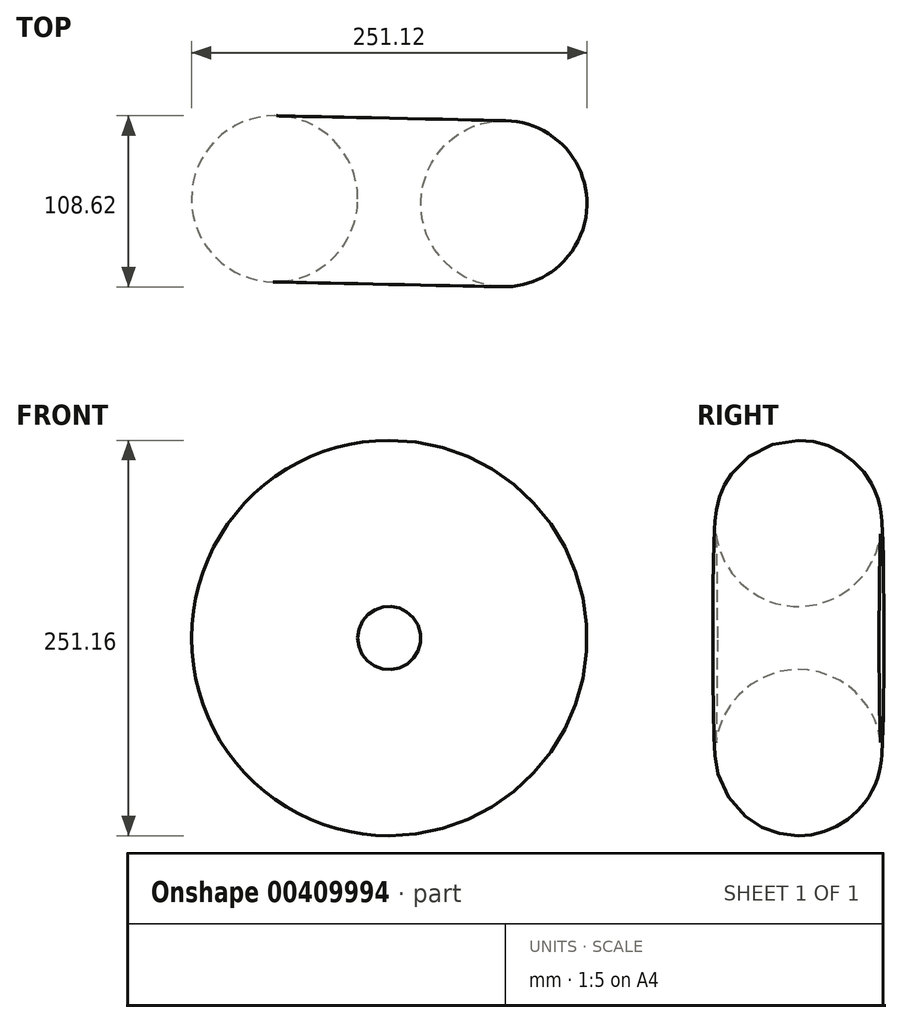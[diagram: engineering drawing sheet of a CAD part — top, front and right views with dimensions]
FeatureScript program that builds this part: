
annotation { "Feature Type Name" : "Feature", "Feature Type Description" : "" }
export const myFeature = defineFeature(function(context is Context, id is Id, definition is map)
    precondition{}
    {
        {
            var Q0;
            Q0=qCreatedBy(makeId("Top.planeOp"),FACE);
            var sketch = newSketch(context, id + "F0", { "sketchPlane" : qUnion([Q0])});
            skCircle(sketch, "E0", {"center": v(0, -10.02) * mm, "radius": 52.77 * mm});
            skCircle(sketch, "E1.cCircle", {"center": v(-20.6, 13.6) * mm, "radius": 6.7 * mm, "construction": true});
            skLineSegment(sketch, "E1.0", {"start": v(-15.87, 18.33) * mm, "end": v(-18.86, 7.13) * mm});
            skLineSegment(sketch, "E1.1", {"start": v(-18.86, 7.13) * mm, "end": v(-27.07, 15.33) * mm});
            skLineSegment(sketch, "E1.2", {"start": v(-27.07, 15.33) * mm, "end": v(-15.87, 18.33) * mm});
            skCircle(sketch, "E2.cCircle", {"center": v(-4.45, 30.32) * mm, "radius": 6.96 * mm, "construction": true});
            skLineSegment(sketch, "E2.0", {"start": v(-2.5, 37) * mm, "end": v(0.36, 25.29) * mm});
            skLineSegment(sketch, "E2.1", {"start": v(0.36, 25.29) * mm, "end": v(-11.21, 28.66) * mm});
            skLineSegment(sketch, "E2.2", {"start": v(-11.21, 28.66) * mm, "end": v(-2.5, 37) * mm});
            skCircle(sketch, "E3.cCircle", {"center": v(3.9, 10.85) * mm, "radius": 7.52 * mm, "construction": true});
            skLineSegment(sketch, "E3.0", {"start": v(3.62, 18.37) * mm, "end": v(10.54, 7.34) * mm});
            skLineSegment(sketch, "E3.1", {"start": v(10.54, 7.34) * mm, "end": v(-2.47, 6.86) * mm});
            skLineSegment(sketch, "E3.2", {"start": v(-2.47, 6.86) * mm, "end": v(3.62, 18.37) * mm});
            skCircle(sketch, "E4.cCircle", {"center": v(25.6, 24.24) * mm, "radius": 6.3 * mm, "construction": true});
            skLineSegment(sketch, "E4.0", {"start": v(23.94, 30.32) * mm, "end": v(31.7, 22.65) * mm});
            skLineSegment(sketch, "E4.1", {"start": v(31.7, 22.65) * mm, "end": v(21.18, 19.76) * mm});
            skLineSegment(sketch, "E4.2", {"start": v(21.18, 19.76) * mm, "end": v(23.94, 30.32) * mm});
            skCircle(sketch, "E5.cCircle", {"center": v(26.44, 3.1) * mm, "radius": 7.15 * mm, "construction": true});
            skLineSegment(sketch, "E5.0", {"start": v(24.77, 10.05) * mm, "end": v(33.3, 1.07) * mm});
            skLineSegment(sketch, "E5.1", {"start": v(33.3, 1.07) * mm, "end": v(21.26, -1.82) * mm});
            skLineSegment(sketch, "E5.2", {"start": v(21.26, -1.82) * mm, "end": v(24.77, 10.05) * mm});
            skCircle(sketch, "E6.cCircle", {"center": v(-38.7, 0) * mm, "radius": 7.06 * mm, "construction": true});
            skLineSegment(sketch, "E6.0", {"start": v(-35.07, 6.06) * mm, "end": v(-35.25, -6.16) * mm});
            skLineSegment(sketch, "E6.1", {"start": v(-35.25, -6.16) * mm, "end": v(-45.75, 0.1) * mm});
            skLineSegment(sketch, "E6.2", {"start": v(-45.75, 0.1) * mm, "end": v(-35.07, 6.06) * mm});
            skCircle(sketch, "E7.cCircle", {"center": v(-13.08, -6.7) * mm, "radius": 6.9 * mm, "construction": true});
            skLineSegment(sketch, "E7.0", {"start": v(-11.41, 0) * mm, "end": v(-8.11, -11.5) * mm});
            skLineSegment(sketch, "E7.1", {"start": v(-8.11, -11.5) * mm, "end": v(-19.72, -8.6) * mm});
            skLineSegment(sketch, "E7.2", {"start": v(-19.72, -8.6) * mm, "end": v(-11.41, 0) * mm});
            skCircle(sketch, "E8.cCircle", {"center": v(-29.5, -21.47) * mm, "radius": 7.05 * mm, "construction": true});
            skLineSegment(sketch, "E8.0", {"start": v(-28.4, -14.52) * mm, "end": v(-24.04, -25.92) * mm});
            skLineSegment(sketch, "E8.1", {"start": v(-24.04, -25.92) * mm, "end": v(-36.09, -23.99) * mm});
            skLineSegment(sketch, "E8.2", {"start": v(-36.09, -23.99) * mm, "end": v(-28.4, -14.52) * mm});
            skCircle(sketch, "E9.cCircle", {"center": v(14.2, -16.67) * mm, "radius": 8.28 * mm, "construction": true});
            skLineSegment(sketch, "E9.0", {"start": v(16.98, -8.88) * mm, "end": v(19.55, -22.98) * mm});
            skLineSegment(sketch, "E9.1", {"start": v(19.55, -22.98) * mm, "end": v(6.05, -18.16) * mm});
            skLineSegment(sketch, "E9.2", {"start": v(6.05, -18.16) * mm, "end": v(16.98, -8.88) * mm});
            skCircle(sketch, "E10.cCircle", {"center": v(-6.68, -28.4) * mm, "radius": 7.28 * mm, "construction": true});
            skLineSegment(sketch, "E10.0", {"start": v(-7.52, -21.16) * mm, "end": v(0, -31.29) * mm});
            skLineSegment(sketch, "E10.1", {"start": v(0, -31.29) * mm, "end": v(-12.53, -32.73) * mm});
            skLineSegment(sketch, "E10.2", {"start": v(-12.53, -32.73) * mm, "end": v(-7.52, -21.16) * mm});
            skCircle(sketch, "E11.cCircle", {"center": v(38.13, -14.69) * mm, "radius": 7.37 * mm, "construction": true});
            skLineSegment(sketch, "E11.0", {"start": v(39.53, -7.45) * mm, "end": v(43.7, -19.51) * mm});
            skLineSegment(sketch, "E11.1", {"start": v(43.7, -19.51) * mm, "end": v(31.17, -17.1) * mm});
            skLineSegment(sketch, "E11.2", {"start": v(31.17, -17.1) * mm, "end": v(39.53, -7.45) * mm});
            skCircle(sketch, "E12.cCircle", {"center": v(33.3, -36.4) * mm, "radius": 7.52 * mm, "construction": true});
            skLineSegment(sketch, "E12.0", {"start": v(33.3, -28.88) * mm, "end": v(39.8, -40.16) * mm});
            skLineSegment(sketch, "E12.1", {"start": v(39.8, -40.16) * mm, "end": v(26.8, -40.16) * mm});
            skLineSegment(sketch, "E12.2", {"start": v(26.8, -40.16) * mm, "end": v(33.3, -28.88) * mm});
            skCircle(sketch, "E13.cCircle", {"center": v(11.97, -37.82) * mm, "radius": 7.61 * mm, "construction": true});
            skLineSegment(sketch, "E13.0", {"start": v(15.87, -31.29) * mm, "end": v(15.68, -44.47) * mm});
            skLineSegment(sketch, "E13.1", {"start": v(15.68, -44.47) * mm, "end": v(4.36, -37.72) * mm});
            skLineSegment(sketch, "E13.2", {"start": v(4.36, -37.72) * mm, "end": v(15.87, -31.29) * mm});
            skCircle(sketch, "E14.cCircle", {"center": v(2.23, -54.8) * mm, "radius": 8.07 * mm, "construction": true});
            skLineSegment(sketch, "E14.0", {"start": v(2.23, -46.74) * mm, "end": v(9.21, -58.84) * mm});
            skLineSegment(sketch, "E14.1", {"start": v(9.21, -58.84) * mm, "end": v(-4.76, -58.84) * mm});
            skLineSegment(sketch, "E14.2", {"start": v(-4.76, -58.84) * mm, "end": v(2.23, -46.74) * mm});
            skCircle(sketch, "E15.cCircle", {"center": v(-14.47, -41.48) * mm, "radius": 6.13 * mm, "construction": true});
            skLineSegment(sketch, "E15.0", {"start": v(-14.2, -35.36) * mm, "end": v(-9.31, -44.78) * mm});
            skLineSegment(sketch, "E15.1", {"start": v(-9.31, -44.78) * mm, "end": v(-19.91, -44.3) * mm});
            skLineSegment(sketch, "E15.2", {"start": v(-19.91, -44.3) * mm, "end": v(-14.2, -35.36) * mm});
            skCircle(sketch, "E16.cCircle", {"center": v(-32.01, -37.06) * mm, "radius": 6 * mm, "construction": true});
            skLineSegment(sketch, "E16.0", {"start": v(-30.34, -31.29) * mm, "end": v(-27.85, -41.4) * mm});
            skLineSegment(sketch, "E16.1", {"start": v(-27.85, -41.4) * mm, "end": v(-37.84, -38.5) * mm});
            skLineSegment(sketch, "E16.2", {"start": v(-37.84, -38.5) * mm, "end": v(-30.34, -31.29) * mm});
            skCircle(sketch, "E17.cCircle", {"center": v(-35.07, 19.76) * mm, "radius": 4.62 * mm, "construction": true});
            skLineSegment(sketch, "E17.0", {"start": v(-33.96, 24.24) * mm, "end": v(-31.75, 16.56) * mm});
            skLineSegment(sketch, "E17.1", {"start": v(-31.75, 16.56) * mm, "end": v(-39.51, 18.48) * mm});
            skLineSegment(sketch, "E17.2", {"start": v(-39.51, 18.48) * mm, "end": v(-33.96, 24.24) * mm});
            skCircle(sketch, "E18.cCircle", {"center": v(-18.93, 30.85) * mm, "radius": 4.8 * mm, "construction": true});
            skLineSegment(sketch, "E18.0", {"start": v(-18.1, 35.58) * mm, "end": v(-15.25, 27.76) * mm});
            skLineSegment(sketch, "E18.1", {"start": v(-15.25, 27.76) * mm, "end": v(-23.44, 29.2) * mm});
            skLineSegment(sketch, "E18.2", {"start": v(-23.44, 29.2) * mm, "end": v(-18.1, 35.58) * mm});
            skCircle(sketch, "E19.cCircle", {"center": v(10.58, 27.56) * mm, "radius": 5.02 * mm, "construction": true});
            skLineSegment(sketch, "E19.0", {"start": v(10.86, 32.57) * mm, "end": v(14.78, 24.81) * mm});
            skLineSegment(sketch, "E19.1", {"start": v(14.78, 24.81) * mm, "end": v(6.1, 25.3) * mm});
            skLineSegment(sketch, "E19.2", {"start": v(6.1, 25.3) * mm, "end": v(10.86, 32.57) * mm});
            skCircle(sketch, "E20.cCircle", {"center": v(40.92, 5.9) * mm, "radius": 4.37 * mm, "construction": true});
            skLineSegment(sketch, "E20.0", {"start": v(39.53, 10.05) * mm, "end": v(45.2, 5.04) * mm});
            skLineSegment(sketch, "E20.1", {"start": v(45.2, 5.04) * mm, "end": v(38.02, 2.63) * mm});
            skLineSegment(sketch, "E20.2", {"start": v(38.02, 2.63) * mm, "end": v(39.53, 10.05) * mm});
            skCircle(sketch, "E21.cCircle", {"center": v(4.45, -3.06) * mm, "radius": 6.6 * mm, "construction": true});
            skLineSegment(sketch, "E21.0", {"start": v(10.3, 0) * mm, "end": v(4.18, -9.65) * mm});
            skLineSegment(sketch, "E21.1", {"start": v(4.18, -9.65) * mm, "end": v(-1.12, 0.48) * mm});
            skLineSegment(sketch, "E21.2", {"start": v(-1.12, 0.48) * mm, "end": v(10.3, 0) * mm});
            skCircle(sketch, "E22.cCircle", {"center": v(-45.1, -13.99) * mm, "radius": 6.35 * mm, "construction": true});
            skLineSegment(sketch, "E22.0", {"start": v(-43.42, -7.86) * mm, "end": v(-40.63, -18.5) * mm});
            skLineSegment(sketch, "E22.1", {"start": v(-40.63, -18.5) * mm, "end": v(-51.23, -15.6) * mm});
            skLineSegment(sketch, "E22.2", {"start": v(-51.23, -15.6) * mm, "end": v(-43.42, -7.86) * mm});
            skCircle(sketch, "E23.cCircle", {"center": v(21.18, -50.6) * mm, "radius": 6.12 * mm, "construction": true});
            skLineSegment(sketch, "E23.0", {"start": v(21.18, -44.48) * mm, "end": v(26.49, -53.67) * mm});
            skLineSegment(sketch, "E23.1", {"start": v(26.49, -53.67) * mm, "end": v(15.88, -53.67) * mm});
            skLineSegment(sketch, "E23.2", {"start": v(15.88, -53.67) * mm, "end": v(21.18, -44.48) * mm});
            skCircle(sketch, "E24.cCircle", {"center": v(-16.14, -53.17) * mm, "radius": 3.71 * mm, "construction": true});
            skLineSegment(sketch, "E24.0", {"start": v(-16.98, -49.55) * mm, "end": v(-12.6, -54.25) * mm});
            skLineSegment(sketch, "E24.1", {"start": v(-12.6, -54.25) * mm, "end": v(-18.86, -55.7) * mm});
            skLineSegment(sketch, "E24.2", {"start": v(-18.86, -55.7) * mm, "end": v(-16.98, -49.55) * mm});
            skLineSegment(sketch, "E25", {"start": v(-71.54, 50.8) * mm, "end": v(-73.76, -54.65) * mm});
            skSolve(sketch);
        }
        {
            var Q0;
            Q0=makeQuery(id+"F0.imprint","IMPRINT",FACE,{"disambiguationData":[TD([[makeQuery(id+"F0.imprint","IMPRINT",EDGE,{"derivedFrom":sQuery(id+"F0.wireOp",EDGE,"E2.0")}),-1.0]])]});
            var Q1;
            Q1=makeQuery(id+"F0.imprint","IMPRINT",FACE,{"disambiguationData":[TD([[makeQuery(id+"F0.imprint","IMPRINT",EDGE,{"derivedFrom":sQuery(id+"F0.wireOp",EDGE,"E3.0")}),-1.0]])]});
            var Q2;
            Q2=makeQuery(id+"F0.imprint","IMPRINT",FACE,{"disambiguationData":[TD([[makeQuery(id+"F0.imprint","IMPRINT",EDGE,{"derivedFrom":sQuery(id+"F0.wireOp",EDGE,"E13.0")}),-1.0]])]});
            var Q3;
            Q3=makeQuery(id+"F0.imprint","IMPRINT",FACE,{"disambiguationData":[TD([[makeQuery(id+"F0.imprint","IMPRINT",EDGE,{"derivedFrom":sQuery(id+"F0.wireOp",EDGE,"E12.0")}),-1.0]])]});
            var Q4;
            Q4=makeQuery(id+"F0.imprint","IMPRINT",FACE,{"disambiguationData":[TD([[makeQuery(id+"F0.imprint","IMPRINT",EDGE,{"derivedFrom":sQuery(id+"F0.wireOp",EDGE,"E11.0")}),-1.0]])]});
            var Q5;
            Q5=makeQuery(id+"F0.imprint","IMPRINT",FACE,{"disambiguationData":[TD([[makeQuery(id+"F0.imprint","IMPRINT",EDGE,{"derivedFrom":sQuery(id+"F0.wireOp",EDGE,"E10.0")}),-1.0]])]});
            var Q6;
            Q6=makeQuery(id+"F0.imprint","IMPRINT",FACE,{"disambiguationData":[TD([[makeQuery(id+"F0.imprint","IMPRINT",EDGE,{"derivedFrom":sQuery(id+"F0.wireOp",EDGE,"E9.0")}),-1.0]])]});
            var Q7;
            Q7=makeQuery(id+"F0.imprint","IMPRINT",FACE,{"disambiguationData":[TD([[makeQuery(id+"F0.imprint","IMPRINT",EDGE,{"derivedFrom":sQuery(id+"F0.wireOp",EDGE,"E8.0")}),-1.0]])]});
            var Q8;
            Q8=makeQuery(id+"F0.imprint","IMPRINT",FACE,{"disambiguationData":[TD([[makeQuery(id+"F0.imprint","IMPRINT",EDGE,{"derivedFrom":sQuery(id+"F0.wireOp",EDGE,"E7.0")}),-1.0]])]});
            var Q9;
            Q9=makeQuery(id+"F0.imprint","IMPRINT",FACE,{"disambiguationData":[TD([[makeQuery(id+"F0.imprint","IMPRINT",EDGE,{"derivedFrom":sQuery(id+"F0.wireOp",EDGE,"E1.0")}),-1.0]])]});
            var Q10;
            Q10=makeQuery(id+"F0.imprint","IMPRINT",FACE,{"disambiguationData":[TD([[makeQuery(id+"F0.imprint","IMPRINT",EDGE,{"derivedFrom":sQuery(id+"F0.wireOp",EDGE,"E5.0")}),-1.0]])]});
            var Q11;
            Q11=makeQuery(id+"F0.imprint","IMPRINT",FACE,{"disambiguationData":[TD([[makeQuery(id+"F0.imprint","IMPRINT",EDGE,{"derivedFrom":sQuery(id+"F0.wireOp",EDGE,"E4.0")}),-1.0]])]});
            var Q12;
            Q12=makeQuery(id+"F0.imprint","IMPRINT",FACE,{"disambiguationData":[TD([[makeQuery(id+"F0.imprint","IMPRINT",EDGE,{"derivedFrom":sQuery(id+"F0.wireOp",EDGE,"E6.0")}),-1.0]])]});
            var Q13;
            Q13=makeQuery(id+"F0.imprint","IMPRINT",FACE,{"disambiguationData":[TD([[makeQuery(id+"F0.imprint","IMPRINT",EDGE,{"derivedFrom":sQuery(id+"F0.wireOp",EDGE,"E22.0")}),-1.0]])]});
            var Q14;
            Q14=makeQuery(id+"F0.imprint","IMPRINT",FACE,{"disambiguationData":[TD([[makeQuery(id+"F0.imprint","IMPRINT",EDGE,{"derivedFrom":sQuery(id+"F0.wireOp",EDGE,"E15.0")}),-1.0]])]});
            var Q15;
            Q15=makeQuery(id+"F0.imprint","IMPRINT",FACE,{"disambiguationData":[TD([[makeQuery(id+"F0.imprint","IMPRINT",EDGE,{"derivedFrom":sQuery(id+"F0.wireOp",EDGE,"E14.0")}),-1.0]])]});
            var Q16;
            Q16=makeQuery(id+"F0.imprint","IMPRINT",FACE,{"disambiguationData":[TD([[makeQuery(id+"F0.imprint","IMPRINT",EDGE,{"derivedFrom":sQuery(id+"F0.wireOp",EDGE,"E16.0")}),-1.0]])]});
            var Q17;
            Q17=makeQuery(id+"F0.imprint","IMPRINT",FACE,{"disambiguationData":[TD([[makeQuery(id+"F0.imprint","IMPRINT",EDGE,{"derivedFrom":sQuery(id+"F0.wireOp",EDGE,"E18.0")}),-1.0]])]});
            var Q18;
            Q18=makeQuery(id+"F0.imprint","IMPRINT",FACE,{"disambiguationData":[TD([[makeQuery(id+"F0.imprint","IMPRINT",EDGE,{"derivedFrom":sQuery(id+"F0.wireOp",EDGE,"E23.0")}),-1.0]])]});
            var Q19;
            Q19=makeQuery(id+"F0.imprint","IMPRINT",FACE,{"disambiguationData":[TD([[makeQuery(id+"F0.imprint","IMPRINT",EDGE,{"derivedFrom":sQuery(id+"F0.wireOp",EDGE,"E0")}),1.0]])]});
            var Q20;
            Q20=makeQuery(id+"F0.imprint","IMPRINT",FACE,{"disambiguationData":[TD([[makeQuery(id+"F0.imprint","IMPRINT",EDGE,{"derivedFrom":sQuery(id+"F0.wireOp",EDGE,"E19.0")}),-1.0]])]});
            var Q21;
            Q21=makeQuery(id+"F0.imprint","IMPRINT",FACE,{"disambiguationData":[TD([[makeQuery(id+"F0.imprint","IMPRINT",EDGE,{"derivedFrom":sQuery(id+"F0.wireOp",EDGE,"E21.0")}),-1.0]])]});
            var Q22;
            Q22=makeQuery(id+"F0.imprint","IMPRINT",FACE,{"disambiguationData":[TD([[makeQuery(id+"F0.imprint","IMPRINT",EDGE,{"derivedFrom":sQuery(id+"F0.wireOp",EDGE,"E24.0")}),-1.0]])]});
            var Q23;
            Q23=makeQuery(id+"F0.imprint","IMPRINT",FACE,{"disambiguationData":[TD([[makeQuery(id+"F0.imprint","IMPRINT",EDGE,{"derivedFrom":sQuery(id+"F0.wireOp",EDGE,"E17.0")}),-1.0]])]});
            var Q24;
            Q24=makeQuery(id+"F0.imprint","IMPRINT",FACE,{"disambiguationData":[TD([[makeQuery(id+"F0.imprint","IMPRINT",EDGE,{"derivedFrom":sQuery(id+"F0.wireOp",EDGE,"E20.0")}),-1.0]])]});
            var Q25;
            Q25=sQuery(id+"F0.wireOp",EDGE,"E25");
            revolve(context, id + "F1", {"entities" : qUnion([Q0, Q1, Q2, Q3, Q4, Q5, Q6, Q7, Q8, Q9, Q10, Q11, Q12, Q13, Q14, Q15, Q16, Q17, Q18, Q19, Q20, Q21, Q22, Q23, Q24]), "axis" : qUnion([Q25]), "revolveType" : RevolveType.FULL});
        }
    });
